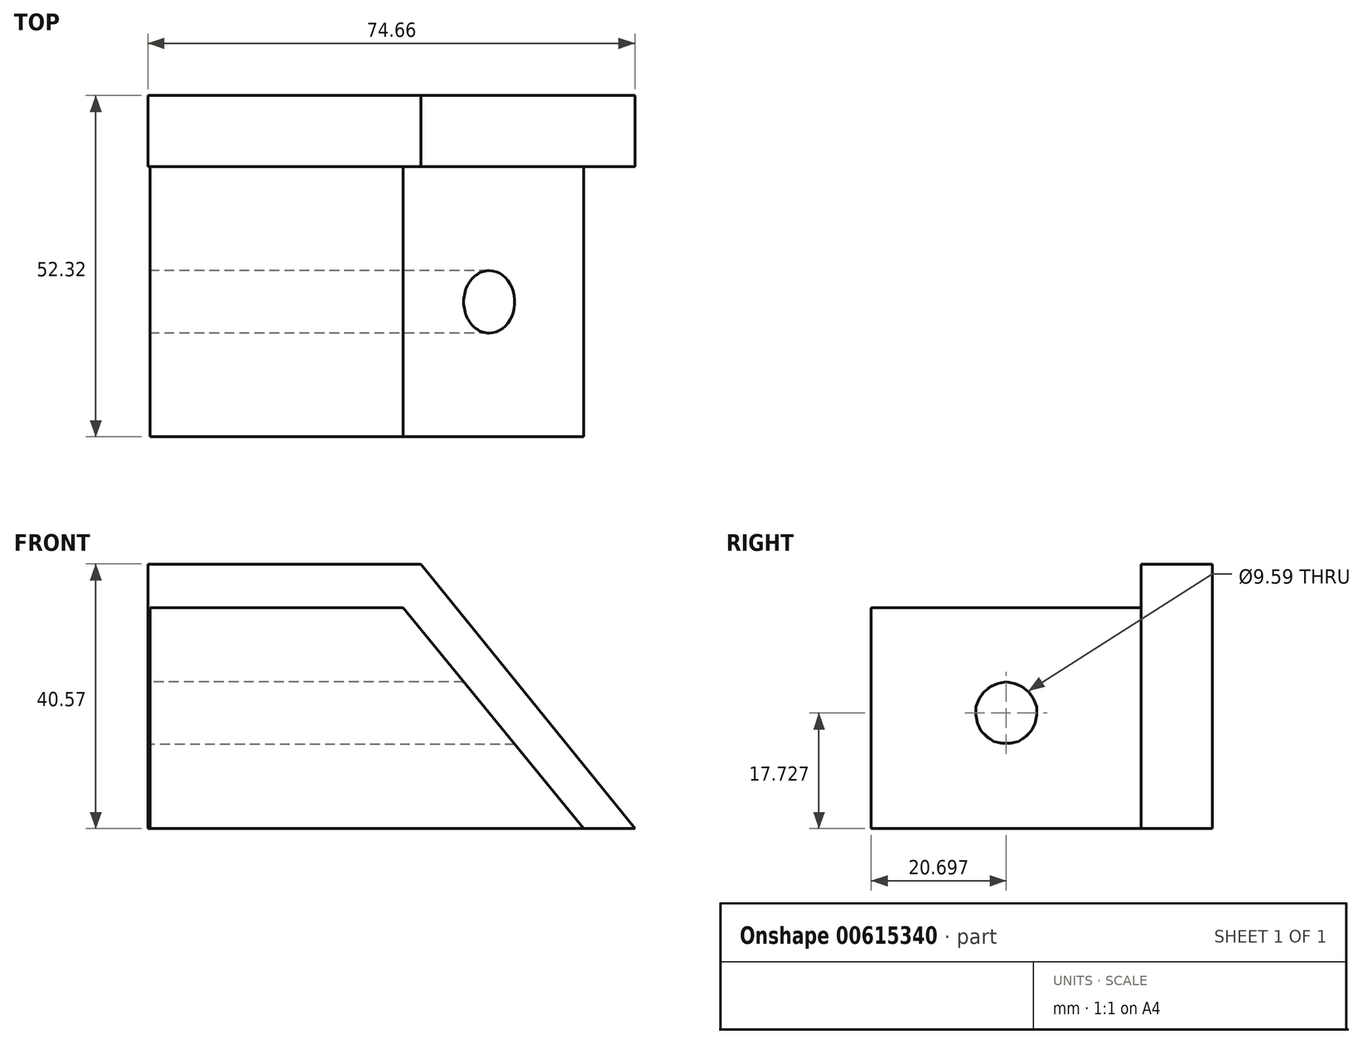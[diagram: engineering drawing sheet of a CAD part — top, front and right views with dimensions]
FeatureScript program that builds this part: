
annotation { "Feature Type Name" : "Feature", "Feature Type Description" : "" }
export const myFeature = defineFeature(function(context is Context, id is Id, definition is map)
    precondition{}
    {
        {
            var Q0;
            Q0=qCreatedBy(makeId("Front.planeOp"),FACE);
            var sketch = newSketch(context, id + "F0", { "sketchPlane" : qUnion([Q0])});
            skLineSegment(sketch, "E0", {"start": v(-29.65, 0) * mm, "end": v(-29.65, 33.87) * mm});
            skLineSegment(sketch, "E1", {"start": v(-29.65, 33.87) * mm, "end": v(9.18, 33.87) * mm});
            skLineSegment(sketch, "E2", {"start": v(9.18, 33.87) * mm, "end": v(36.88, 0) * mm});
            skLineSegment(sketch, "E3", {"start": v(36.88, 0) * mm, "end": v(-29.65, 0) * mm});
            skSolve(sketch);
        }
        {
            var Q0;
            Q0 = qSketchRegion(id + "F0", true);
            extrude(context, id + "F1", {"entities" : qUnion([Q0]), "depth" : 40.64 * mm, "offsetDistance" : 25.4 * mm});
        }
        {
            var Q0;
            Q0=qCreatedBy(makeId("Front.planeOp"),FACE);
            var sketch = newSketch(context, id + "F2", { "sketchPlane" : qUnion([Q0])});
            skLineSegment(sketch, "E4", {"start": v(-29.95, 34.24) * mm, "end": v(-29.95, 40.57) * mm});
            skLineSegment(sketch, "E5", {"start": v(-29.95, 40.57) * mm, "end": v(11.9, 40.57) * mm});
            skLineSegment(sketch, "E6", {"start": v(11.9, 40.57) * mm, "end": v(44.7, 0) * mm});
            skLineSegment(sketch, "E7", {"start": v(44.7, 0) * mm, "end": v(-29.95, 0) * mm});
            skLineSegment(sketch, "E8", {"start": v(-29.95, 0) * mm, "end": v(-29.95, 40.57) * mm});
            skSolve(sketch);
        }
        {
            var Q0;
            {var subQ0=sQuery(id+"F2.wireOp",EDGE,"E5");Q0=makeQuery(id+"F2.imprint","IMPRINT",FACE,{"disambiguationData":[TD([[makeQuery(id+"F2.imprint","IMPRINT",EDGE,{"derivedFrom":subQ0}),-1.0]])]});}
            extrude(context, id + "F3", {"entities" : qUnion([Q0]), "operationType" : NewBodyOperationType.ADD, "depth" : 10.92 * mm, "offsetDistance" : 25.4 * mm});
        }
        {
            var Q0;
            Q0=makeQuery(id+"F1.opExtrude","CAP_FACE",FACE,{"disambiguationData":[OSD([sQuery(id+"F0.wireOp",EDGE,"E0"),sQuery(id+"F0.wireOp",EDGE,"E1"),sQuery(id+"F0.wireOp",EDGE,"E2"),sQuery(id+"F0.wireOp",EDGE,"E3")])],"isStart":false});
            extrude(context, id + "F4", {"entities" : qUnion([Q0]), "operationType" : NewBodyOperationType.ADD, "depth" : 11.68 * mm, "offsetDistance" : 25.4 * mm});
        }
        {
            var Q0;
            {var subQ0=sQuery(id+"F0.wireOp",EDGE,"E0");Q0=makeQuery(id+"F4.boolean.opBoolean","MERGE",FACE,{"derivedFrom":[makeQuery(id+"F1.opExtrude","SWEPT_FACE",FACE,{"disambiguationData":[OSD([subQ0])]}),makeQuery(id+"F4.opExtrude","SWEPT_FACE",FACE,{"disambiguationData":[OSD([subQ0])]})]});}
            var sketch = newSketch(context, id + "F5", { "sketchPlane" : qUnion([Q0])});
            skCircle(sketch, "E9", {"center": v(31.62, 17.73) * mm, "radius": 4.8 * mm});
            skPoint(sketch, "E9.centerSnap0", {"position": v(31.62, 33.87) * mm});
            skSolve(sketch);
        }
        {
            var Q0;
            Q0=makeQuery(id+"F5.imprint","IMPRINT",FACE,{"disambiguationData":[TD([[makeQuery(id+"F5.imprint","IMPRINT",EDGE,{"derivedFrom":sQuery(id+"F5.wireOp",EDGE,"E9")}),1.0]])]});
            extrude(context, id + "F6", {"entities" : qUnion([Q0]), "operationType" : NewBodyOperationType.REMOVE, "oppositeDirection" : true, "depth" : 104.14 * mm, "offsetDistance" : 25.4 * mm});
        }
    });
